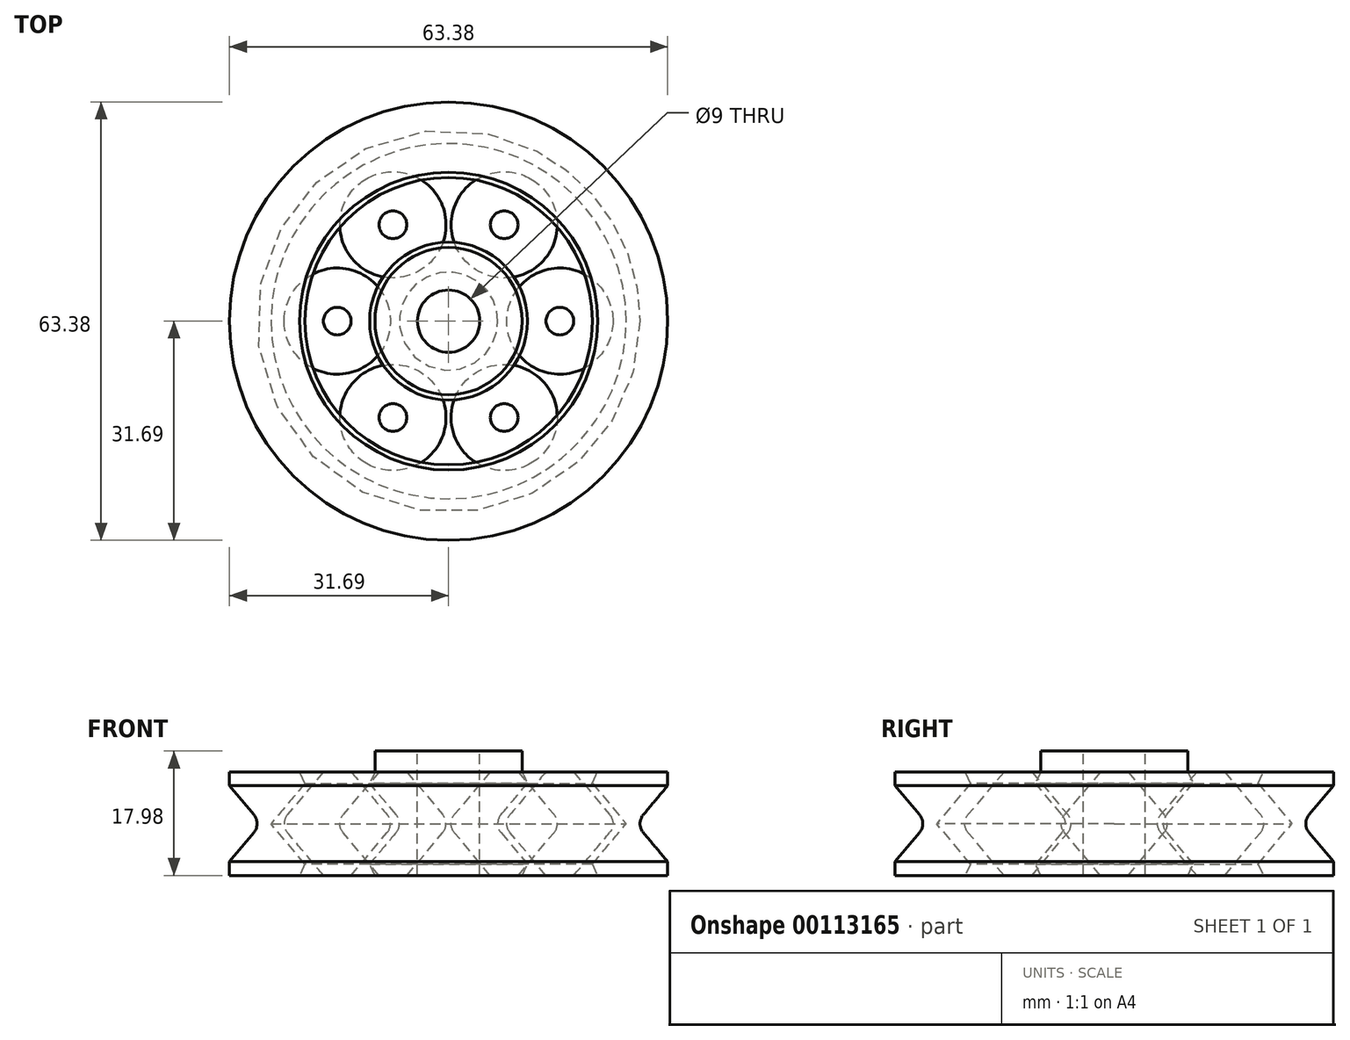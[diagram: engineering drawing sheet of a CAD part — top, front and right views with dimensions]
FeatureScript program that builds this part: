
annotation { "Feature Type Name" : "Feature", "Feature Type Description" : "" }
export const myFeature = defineFeature(function(context is Context, id is Id, definition is map)
    precondition{}
    {
        {
            assignVariable(context, id + "F0", {"name" : "LAYER", "anyValue" : 0.4});
        }
        {
            assignVariable(context, id + "F1", {"name" : "WALL", "anyValue" : getVariable(context, 'LAYER') * 5});
        }
        {
            assignVariable(context, id + "F2", {"name" : "GAP", "anyValue" : 1});
        }
        {
            var Q0;
            Q0=qCreatedBy(makeId("Front.planeOp"),FACE);
            var sketch = newSketch(context, id + "F3", { "sketchPlane" : qUnion([Q0])});
            skLineSegment(sketch, "E0", {"start": v(0, 7.5) * mm, "end": v(0, -7.5) * mm});
            skLineSegment(sketch, "E1", {"start": v(-6.5, 0) * mm, "end": v(-12.79, 7.5) * mm});
            skLineSegment(sketch, "E2", {"start": v(-4.5, 0) * mm, "end": v(-4.5, 7.5) * mm});
            skLineSegment(sketch, "E3", {"start": v(-7.8, 0) * mm, "end": v(-14.1, 7.5) * mm});
            skLineSegment(sketch, "E4", {"start": v(-4.5, 7.5) * mm, "end": v(-12.79, 7.5) * mm});
            skLineSegment(sketch, "E5", {"start": v(-18.1, 7.5) * mm, "end": v(-24.38, 0) * mm});
            skLineSegment(sketch, "E6", {"start": v(-19.4, 7.5) * mm, "end": v(-31.69, 7.5) * mm});
            skLineSegment(sketch, "E7", {"start": v(-27.69, 0) * mm, "end": v(-25.69, 0) * mm});
            skLineSegment(sketch, "E8", {"start": v(-24.38, 0) * mm, "end": v(-7.8, 0) * mm});
            skLineSegment(sketch, "E9", {"start": v(-6.5, 0) * mm, "end": v(-4.5, 0) * mm});
            skLineSegment(sketch, "E10", {"start": v(-16.1, 7.5) * mm, "end": v(-16.1, 0) * mm});
            skLineSegment(sketch, "E11", {"start": v(-19.4, 7.5) * mm, "end": v(-25.69, 0) * mm});
            skLineSegment(sketch, "E12", {"start": v(-31.69, 7.5) * mm, "end": v(-31.69, 5.5) * mm});
            skLineSegment(sketch, "E13", {"start": v(-31.69, 5.5) * mm, "end": v(-28.16, 1.29) * mm});
            skArc(sketch, "E14", {"start": v(-27.69, 0) * mm, "mid": v(-27.8, 0.68) * mm, "end": v(-28.16, 1.29) * mm});
            skCircle(sketch, "E15", {"center": v(-29.69, 0) * mm, "radius": 2 * mm, "construction": true});
            skLineSegment(sketch, "E16", {"start": v(-18.1, 7.5) * mm, "end": v(-14.1, 7.5) * mm});
            skSolve(sketch);
        }
        {
            var Q0;
            Q0=makeQuery(id+"F3.imprint","IMPRINT",FACE,{"disambiguationData":[TD([[makeQuery(id+"F3.imprint","IMPRINT",EDGE,{"derivedFrom":sQuery(id+"F3.wireOp",EDGE,"E6")}),1.0]])]});
            var Q1;
            Q1=makeQuery(id+"F3.imprint","IMPRINT",FACE,{"disambiguationData":[TD([[makeQuery(id+"F3.imprint","IMPRINT",EDGE,{"derivedFrom":sQuery(id+"F3.wireOp",EDGE,"E1")}),-1.0]])]});
            var Q2;
            Q2=sQuery(id+"F3.wireOp",EDGE,"E0");
            revolve(context, id + "F4", {"entities" : qUnion([Q0, Q1]), "axis" : qUnion([Q2]), "revolveType" : RevolveType.FULL});
        }
        {
            var Q0;
            {var subQ2=sQuery(id+"F3.wireOp",EDGE,"E5");Q0=makeQuery(id+"F3.imprint","IMPRINT",FACE,{"disambiguationData":[TD([[makeQuery(id+"F3.imprint","IMPRINT",EDGE,{"derivedFrom":subQ2}),1.0]])]});}
            var Q1;
            Q1=sQuery(id+"F3.wireOp",EDGE,"E10");
            revolve(context, id + "F5", {"entities" : qUnion([Q0]), "axis" : qUnion([Q1]), "revolveType" : RevolveType.FULL});
        }
        {
            var Q0;
            Q0=makeQuery(id+"F4.opRevolve","SWEPT_BODY",BODY,{"disambiguationData":[OSD([sQuery(id+"F3.wireOp",EDGE,"E1"),sQuery(id+"F3.wireOp",EDGE,"E2"),sQuery(id+"F3.wireOp",EDGE,"6b12b860-28fe-4edf-b4da-5e85ff0cb9de"),sQuery(id+"F3.wireOp",EDGE,"E4"),sQuery(id+"F3.wireOp",EDGE,"E9")])]});
            var Q1;
            Q1=makeQuery(id+"F4.opRevolve","SWEPT_BODY",BODY,{"disambiguationData":[OSD([sQuery(id+"F3.wireOp",EDGE,"8deebb57-5a25-4ce3-9d07-cb33f18be781"),sQuery(id+"F3.wireOp",EDGE,"7ebc7e1d-18b6-46b7-a97a-6a8bf93046ea"),sQuery(id+"F3.wireOp",EDGE,"E6"),sQuery(id+"F3.wireOp",EDGE,"e09d1bc7-0d9d-49fa-a6c3-8106b6049b82"),sQuery(id+"F3.wireOp",EDGE,"E7")])]});
            var Q2;
            Q2=makeQuery(id+"F5.opRevolve","SWEPT_BODY",BODY,{"disambiguationData":[OSD([sQuery(id+"F3.wireOp",EDGE,"e5f09cbf-52d0-439a-958d-7bea0554b5a7"),sQuery(id+"F3.wireOp",EDGE,"525855ad-4003-48c4-92aa-5226f1343de6"),sQuery(id+"F3.wireOp",EDGE,"E5"),sQuery(id+"F3.wireOp",EDGE,"E8"),sQuery(id+"F3.wireOp",EDGE,"E10")])]});
            var Q3;
            Q3=makeQuery(id+"F4.opRevolve","SWEPT_FACE",FACE,{"disambiguationData":[OSD([sQuery(id+"F3.wireOp",EDGE,"E9")])]});
            mirror(context, id + "F6", {"operationType" : NewBodyOperationType.ADD, "entities" : qUnion([Q0, Q1, Q2]), "mirrorPlane" : qUnion([Q3])});
        }
        {
            var Q0;
            {var subQ0=makeQuery(id+"F5.opRevolve","SWEPT_EDGE",EDGE,{"disambiguationData":[OSD([sQuery(id+"F3.wireOp",EDGE,"E5"),sQuery(id+"F3.wireOp",EDGE,"E8")])]});Q0=makeQuery(id+"F6.boolean.opBoolean","MERGE",EDGE,{"derivedFrom":[subQ0,makeQuery(id+"F6.opPattern","COPY",EDGE,{"derivedFrom":subQ0,"instanceName":"1"})]});}
            var Q1;
            {var subQ0=makeQuery(id+"F4.opRevolve","SWEPT_EDGE",EDGE,{"disambiguationData":[OSD([sQuery(id+"F3.wireOp",EDGE,"E1"),sQuery(id+"F3.wireOp",EDGE,"E9")])]});Q1=makeQuery(id+"F6.boolean.opBoolean","MERGE",EDGE,{"derivedFrom":[subQ0,makeQuery(id+"F6.opPattern","COPY",EDGE,{"derivedFrom":subQ0,"instanceName":"1"})]});}
            fillet(context, id + "F7", {"entities" : qUnion([Q0, Q1]), "radius" : (getVariable(context, 'WALL')) * mm, "tangentPropagation" : true, "allowEdgeOverflow" : false});
        }
        {
            var Q0;
            Q0=makeQuery(id+"F5.opRevolve","SWEPT_BODY",BODY,{"disambiguationData":[OSD([sQuery(id+"F3.wireOp",EDGE,"e5f09cbf-52d0-439a-958d-7bea0554b5a7"),sQuery(id+"F3.wireOp",EDGE,"525855ad-4003-48c4-92aa-5226f1343de6"),sQuery(id+"F3.wireOp",EDGE,"E5"),sQuery(id+"F3.wireOp",EDGE,"E8"),sQuery(id+"F3.wireOp",EDGE,"E10")])]});
            var Q1;
            Q1=sQuery(id+"F3.wireOp",EDGE,"E0");
            circularPattern(context, id + "F8", {"entities" : qUnion([Q0]), "axis" : qUnion([Q1]), "angle" : 60 * degree, "instanceCount" : 6});
        }
        {
            var Q0;
            Q0=makeQuery(id+"F4.opRevolve","SWEPT_EDGE",EDGE,{"disambiguationData":[OSD([sQuery(id+"F3.wireOp",EDGE,"E1"),sQuery(id+"F3.wireOp",EDGE,"E4")])]});
            var Q1;
            Q1=makeQuery(id+"F4.opRevolve","SWEPT_EDGE",EDGE,{"disambiguationData":[OSD([sQuery(id+"F3.wireOp",EDGE,"E6"),sQuery(id+"F3.wireOp",EDGE,"E11")])]});
            var Q2;
            Q2=makeQuery(id+"F6.opPattern","COPY",EDGE,{"derivedFrom":makeQuery(id+"F4.opRevolve","SWEPT_EDGE",EDGE,{"disambiguationData":[OSD([sQuery(id+"F3.wireOp",EDGE,"E6"),sQuery(id+"F3.wireOp",EDGE,"E11")])]}),"instanceName":"1"});
            var Q3;
            Q3=makeQuery(id+"F6.opPattern","COPY",EDGE,{"derivedFrom":makeQuery(id+"F4.opRevolve","SWEPT_EDGE",EDGE,{"disambiguationData":[OSD([sQuery(id+"F3.wireOp",EDGE,"E1"),sQuery(id+"F3.wireOp",EDGE,"E4")])]}),"instanceName":"1"});
            chamfer(context, id + "F9", {"entities" : qUnion([Q0, Q1, Q2, Q3]), "width" : 1 * mm, "tangentPropagation" : true});
        }
        {
            var Q0;
            Q0=makeQuery(id+"F4.opRevolve","SWEPT_FACE",FACE,{"disambiguationData":[OSD([sQuery(id+"F3.wireOp",EDGE,"E4")])]});
            extrude(context, id + "F10", {"entities" : qUnion([Q0]), "operationType" : NewBodyOperationType.ADD, "depth" : (getVariable(context, 'WALL') + getVariable(context, 'GAP')) * mm});
        }
    });
